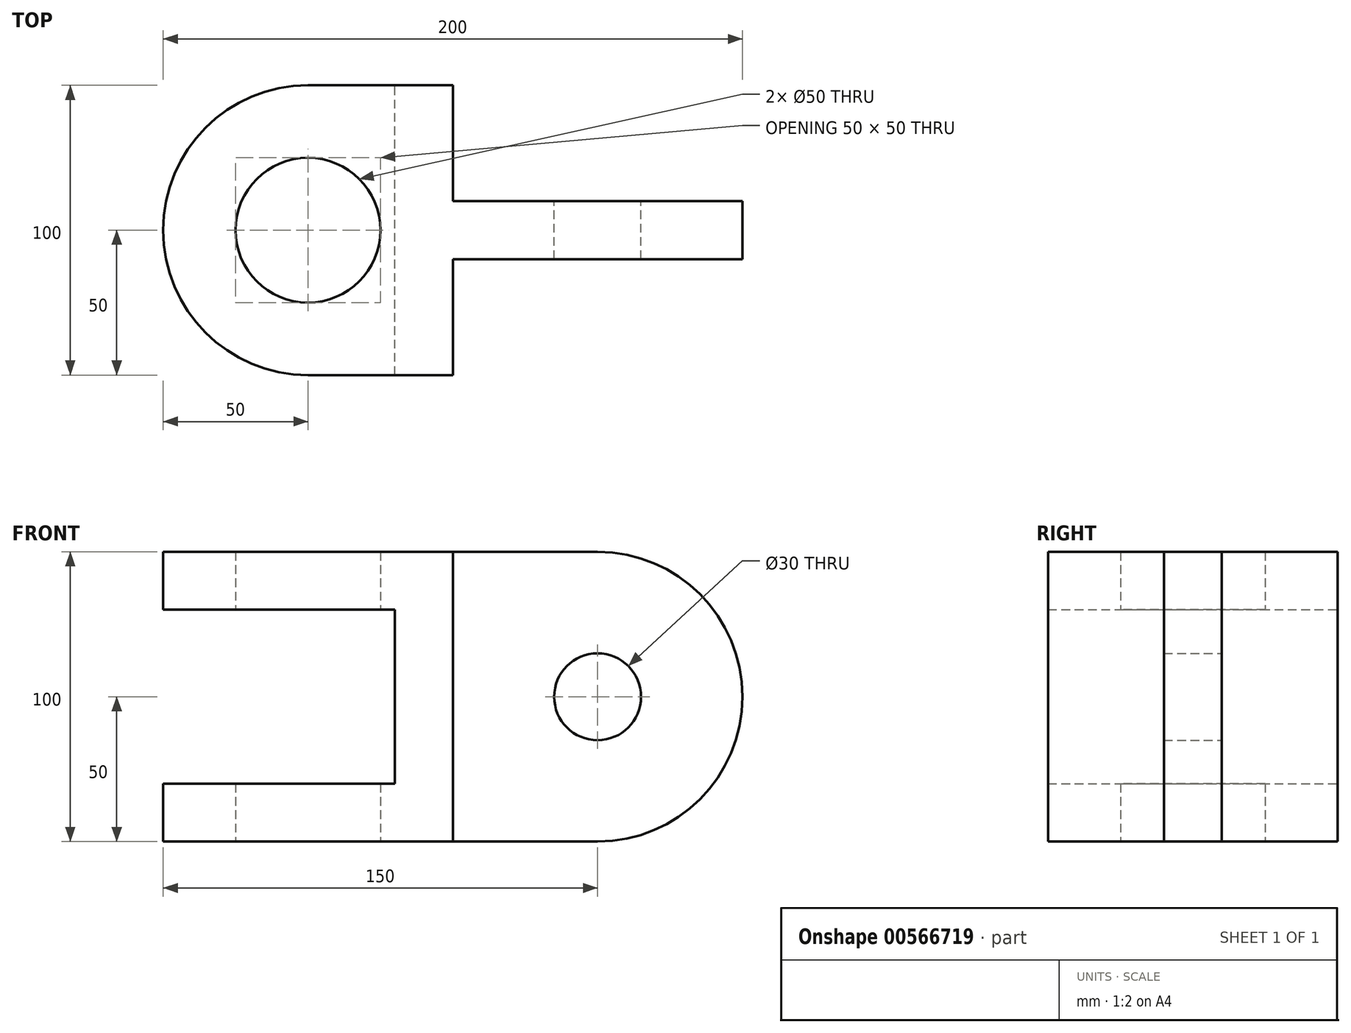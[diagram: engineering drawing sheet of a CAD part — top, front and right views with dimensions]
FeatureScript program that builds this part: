
annotation { "Feature Type Name" : "Feature", "Feature Type Description" : "" }
export const myFeature = defineFeature(function(context is Context, id is Id, definition is map)
    precondition{}
    {
        {
            var Q0;
            Q0=qCreatedBy(makeId("Top.planeOp"),FACE);
            var sketch = newSketch(context, id + "F0", { "sketchPlane" : qUnion([Q0])});
            skLineSegment(sketch, "E0", {"start": v(-50, 50) * mm, "end": v(0, 50) * mm});
            skLineSegment(sketch, "E1", {"start": v(0, 50) * mm, "end": v(0, -50) * mm});
            skLineSegment(sketch, "E2", {"start": v(0, -50) * mm, "end": v(-50, -50) * mm});
            skArc(sketch, "E3", {"start": v(-50, 50) * mm, "mid": v(-100, 0) * mm, "end": v(-50, -50) * mm});
            skCircle(sketch, "E4", {"center": v(-50, 0) * mm, "radius": 25 * mm});
            skLineSegment(sketch, "E5", {"start": v(0, -66.05) * mm, "end": v(0, 74.78) * mm, "construction": true});
            skLineSegment(sketch, "E6", {"start": v(-134.56, 0) * mm, "end": v(86.13, 0) * mm, "construction": true});
            skSolve(sketch);
        }
        {
            var Q0;
            Q0 = qSketchRegion(id + "F0", true);
            extrude(context, id + "F1", {"entities" : qUnion([Q0]), "endBound" : BoundingType.SYMMETRIC, "depth" : 100 * mm, "offsetDistance" : 25 * mm});
        }
        {
            var Q0;
            Q0=qCreatedBy(makeId("Front.planeOp"),FACE);
            var sketch = newSketch(context, id + "F2", { "sketchPlane" : qUnion([Q0])});
            skLineSegment(sketch, "E7", {"start": v(50, -50) * mm, "end": v(0, -50) * mm});
            skLineSegment(sketch, "E8", {"start": v(0, -50) * mm, "end": v(0, 50) * mm});
            skLineSegment(sketch, "E9", {"start": v(0, 50) * mm, "end": v(50, 50) * mm});
            skArc(sketch, "E10", {"start": v(50, -50) * mm, "mid": v(100, 0) * mm, "end": v(50, 50) * mm});
            skCircle(sketch, "E11", {"center": v(50, 0) * mm, "radius": 15 * mm});
            skLineSegment(sketch, "E12", {"start": v(0, 0) * mm, "end": v(127.72, 0) * mm, "construction": true});
            skSolve(sketch);
        }
        {
            var Q0;
            Q0 = qSketchRegion(id + "F2", true);
            extrude(context, id + "F3", {"entities" : qUnion([Q0]), "operationType" : NewBodyOperationType.ADD, "endBound" : BoundingType.SYMMETRIC, "depth" : 20 * mm, "offsetDistance" : 25 * mm});
        }
        {
            var Q0;
            Q0=qCreatedBy(makeId("Front.planeOp"),FACE);
            var sketch = newSketch(context, id + "F4", { "sketchPlane" : qUnion([Q0])});
            skLineSegment(sketch, "E13", {"start": v(-100, -30) * mm, "end": v(-100, 30) * mm});
            skLineSegment(sketch, "E14.bottom", {"start": v(-20, 30) * mm, "end": v(-100, 30) * mm});
            skLineSegment(sketch, "E14.top", {"start": v(-20, -30) * mm, "end": v(-100, -30) * mm});
            skPoint(sketch, "E15.0.2.start.orphan", {"position": v(0, 50) * mm});
            skPoint(sketch, "E16.orphan", {"position": v(-50, -50) * mm});
            skPoint(sketch, "E17.orphan", {"position": v(0, -50) * mm});
            skPoint(sketch, "E15.0.3.start.orphan", {"position": v(-50, 50) * mm});
            skLineSegment(sketch, "E18", {"start": v(-20, 30) * mm, "end": v(-20, -30) * mm});
            skSolve(sketch);
        }
        {
            var Q0;
            Q0 = qSketchRegion(id + "F4", true);
            extrude(context, id + "F5", {"entities" : qUnion([Q0]), "operationType" : NewBodyOperationType.REMOVE, "endBound" : BoundingType.SYMMETRIC, "depth" : 200 * mm, "offsetDistance" : 25 * mm});
        }
    });
